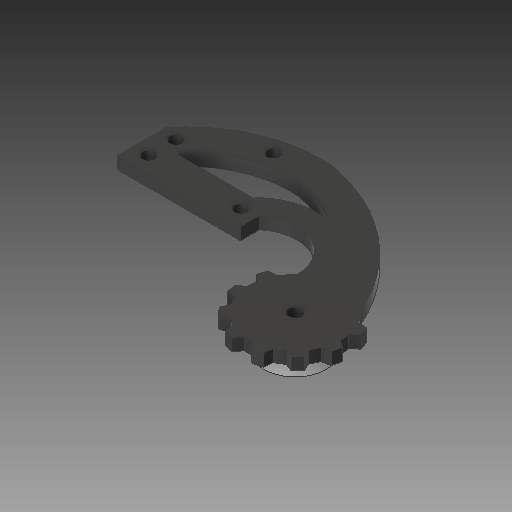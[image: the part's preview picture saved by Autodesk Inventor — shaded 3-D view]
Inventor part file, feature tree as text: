
AUTODESK INVENTOR PART (.ipt)
format: ipt  version: 2017 (Build 210142000, 142)  size: 353,792 bytes
history: native  units: mm
features: sketch x5, extrude x3, hole x2
ambient origin geometry x8: Origin, YZ Plane, XZ Plane, XY Plane, X Axis, Y Axis, Z Axis, Center Point
bodies: Solide1 (feature_tree)
feature tree (10):
  extrude  "Extrusion1"  Depth=10.0mm TaperAngle=90.0deg
  extrude  "Extrusion2"  Depth=4.0mm TaperAngle=0.0deg
  hole  "Perçage1"  [1 undecoded]
  hole  "Perçage2"  [1 undecoded]
  extrude  "Extrusion3"  Depth=20.0mm
  sketch  "Esquisse1"
  sketch  "Esquisse2"
  sketch  "Esquisse3"
  sketch  "Esquisse4"
  sketch  "Esquisse5"
note: 2 required parameter values undecoded (feature->parameter linkage not recoverable at this tier; creation-order binding heuristic only, values carry confidence <= 0.55)
